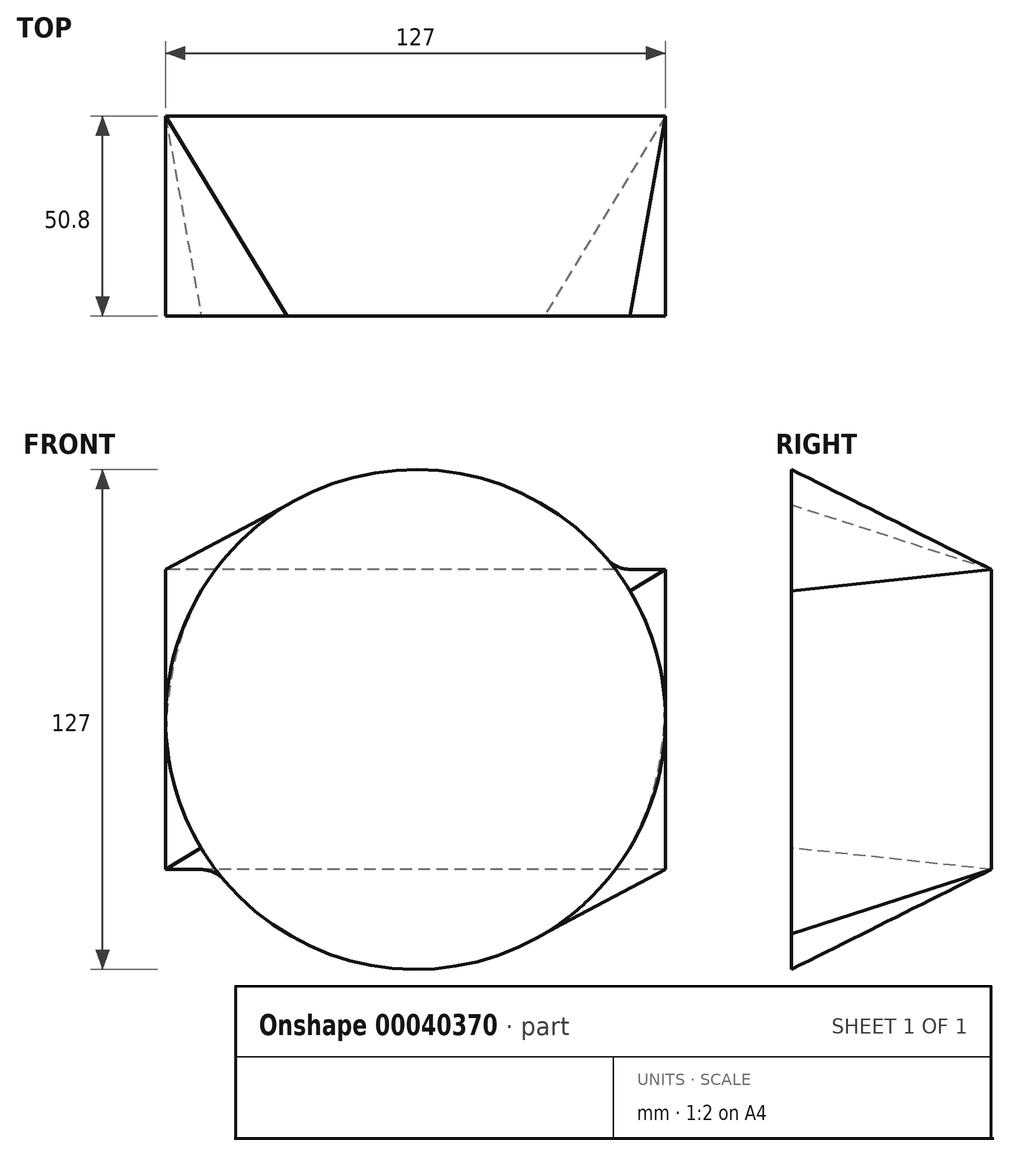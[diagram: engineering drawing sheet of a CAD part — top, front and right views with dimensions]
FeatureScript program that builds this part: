
annotation { "Feature Type Name" : "Feature", "Feature Type Description" : "" }
export const myFeature = defineFeature(function(context is Context, id is Id, definition is map)
    precondition{}
    {
        {
            var Q0;
            Q0=qCreatedBy(makeId("Front.planeOp"),FACE);
            var sketch = newSketch(context, id + "F0", { "sketchPlane" : qUnion([Q0])});
            skLineSegment(sketch, "E0.rect.bottom", {"start": v(63.5, 38.1) * mm, "end": v(-63.5, 38.1) * mm});
            skLineSegment(sketch, "E0.rect.top", {"start": v(63.5, -38.1) * mm, "end": v(-63.5, -38.1) * mm});
            skLineSegment(sketch, "E0.rect.left", {"start": v(63.5, 38.1) * mm, "end": v(63.5, -38.1) * mm});
            skLineSegment(sketch, "E0.rect.right", {"start": v(-63.5, 38.1) * mm, "end": v(-63.5, -38.1) * mm});
            skPoint(sketch, "E0.rect.middle", {"position": v(0, 0) * mm});
            skSolve(sketch);
        }
        {
            var Q0;
            Q0=qCreatedBy(makeId("Front.planeOp"),FACE);
            cPlane(context, id + "F1", {"entities" : qUnion([Q0]), "cplaneType" : CPlaneType.OFFSET, "offset" : 50.8 * mm, "width" : 152.4 * mm, "height" : 152.4 * mm});
        }
        {
            var Q0;
            Q0=qCreatedBy(id+"F1.planeOp",FACE);
            var sketch = newSketch(context, id + "F2", { "sketchPlane" : qUnion([Q0])});
            skCircle(sketch, "E1", {"center": v(0, 0) * mm, "radius": 63.5 * mm});
            skSolve(sketch);
        }
        {
            var Q0;
            Q0 = qSketchRegion(id + "F0", true);
            var Q1;
            Q1 = qSketchRegion(id + "F2", true);
            loft(context, id + "F3", {"sheetProfilesArray" : [{ "sheetProfileEntities" : qUnion([Q0]) }, { "sheetProfileEntities" : qUnion([Q1]) }]});
        }
    });
